# Revit family: Sanitary_Showers_AXOR_12922XXX-AXOR-ShowerSolutions-Basic-set-for-ShowerHeaven_NEW
name_source: partatom
category: Plumbing Fixtures
units: mm (PartAtom-declared; Revit-internal decimal feet)

## family parameters
Cut with Voids When Loaded = No
Host = Face
Maintain Annotation Orientation = No
OmniClass Number = 23.31.15.11
OmniClass Title = Bath Shower Units
Part Type = Normal
Room Calculation Point = No
Round Connector Dimension = Use Diameter
Shared = No

## types (1)
- 12922XXX AXOR ShowerSolutions Basic set for ShowerHeaven 1200/300 4jet with light module
    Connector Description = Water Inlet 12.7mm
    Default Elevation = 1219 mm
    Description = AXOR ShowerSolutions Basic set for ShowerHeaven 1200/300 4jet with light module
    Diameter = 13 mm  [stored 0.0426509 ft]
    Manufacturer = AXOR
    Material 1 = AXOR - Metal - Brass
    Material 2 = AXOR - Metal - Stainless Steel
    Material 3 = AXOR - Plastic - Black
    Material 4 = AXOR - Plastic - Gray
    Model = 12922XXX
    Product Page URL = https://www.axor-design.com
    Product data url = https://bimobject.com
    URL = https://www.axor-design.com
    Version = 1

note: [stored X ft] marks values corroborated as IEEE doubles in the binary element streams (Revit-internal decimal feet)

## geometry (parser evidence)
native form markers: Sweep x2
no freeform markers — native parametric forms only
